# Revit family: DOD-220_Detector óptico convencional
name_source: partatom
category: Dispositivos de alarma de incendios
revit_build: Autodesk Revit 2017 (Build: 20190508_0315(x64)
units: mm (PartAtom-declared; Revit-internal decimal feet)

## family parameters
Anfitrión = Cara
Compartido = No
Corte con vacíos al cargar = No
Cota de conector redondo = Diámetro de uso
Mantener orientación de anotación = No
Punto de cálculo de habitación = No
Tipo de pieza = Normal

## types (1)
- DOD-220
    Altura = 100 mm
    Anchura = 100 mm
    Carga eléctrica = Otro
    Certificación = EN 54-7
    Comentarios de tipo = El detector de incendios de Detnov ha sido desarrollado para asegurar una rápida reacción a los incendios, cumpliendo los máximos estándares de calidad y certificación requeridos en el mercado. Una fiabilidad única a la hora de detectar y proteger las instalaciones para reducir las falsas alarmas, siendo apropiados para las aplicaciones más exigentes.
    Conexionado = 2 x 1,5 mm² trenzado y conexión a base Z-200
    Consumo en alarma = < 100 mA
    Consumo en reposo = < 100 μA
    Cuerpo = ABS
    Código de montaje = PDETDOD-220
    Descripción = Detector óptico de humo convencional con led indicador de estado y salida para piloto remoto, sistema anti hurto. Marca Detnov, modelo DOD-220. Color blanco. Precisa base de conexión Z-200 o Z-200-H. Certificado CPR EN54-7. Dimensiones: 100 x 40 mm.
    Elevación por defecto = 1219 mm
    Fabricante = Detnov Security
    Fases = 1
    Humedad relativa = 95% sin condensación
    Imagen de tipo = <Ninguno>
    Modelo = Detector DOD-220
    Potencia total = 0 VA
    Profundidad = 42 mm
    Teléfono = (+34) 93 371 60 25
    Temperatura trabajo = De -10ºC a 70ºC
    Tensión de trabajo = De 9 a 38VCC
    URL = https://www.detnov.com
    Voltaje = 230 V
    Índice IP = IP40
